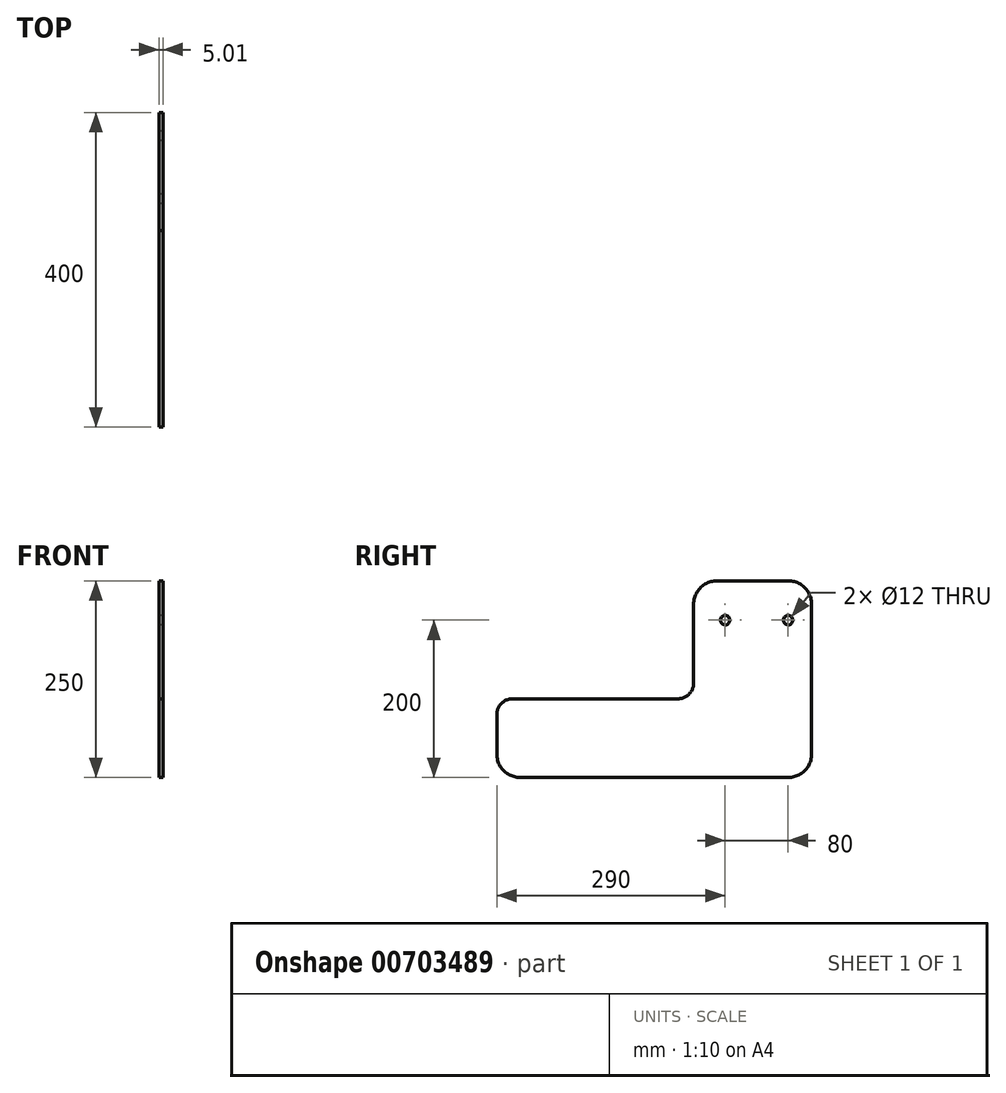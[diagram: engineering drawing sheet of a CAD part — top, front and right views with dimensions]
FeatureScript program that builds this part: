
annotation { "Feature Type Name" : "Feature", "Feature Type Description" : "" }
export const myFeature = defineFeature(function(context is Context, id is Id, definition is map)
    precondition{}
    {
        {
            var Q0;
            Q0=qCreatedBy(makeId("Top.planeOp"),FACE);
            var sketch = newSketch(context, id + "F0", { "sketchPlane" : qUnion([Q0])});
            skArc(sketch, "E0", {"start": v(-28.38, 31.77) * mm, "mid": v(-28.38, 31.77) * mm, "end": v(-28.38, 31.77) * mm});
            skLineSegment(sketch, "E1", {"start": v(-39.18, 36.77) * mm, "end": v(120.46, 36.77) * mm});
            skLineSegment(sketch, "E2", {"start": v(-54.54, 20.82) * mm, "end": v(-54.54, -83.23) * mm});
            skArc(sketch, "E3.0", {"start": v(-39.34, 31.77) * mm, "mid": v(-46.28, 29.18) * mm, "end": v(-49.54, 22.53) * mm});
            skLineSegment(sketch, "E4", {"start": v(-49.54, 22.53) * mm, "end": v(-49.54, -83.23) * mm});
            skLineSegment(sketch, "E5", {"start": v(-49.54, -83.23) * mm, "end": v(-54.54, -83.23) * mm});
            skLineSegment(sketch, "E6", {"start": v(-39.34, 31.77) * mm, "end": v(120.46, 31.77) * mm});
            skLineSegment(sketch, "E7", {"start": v(120.46, 31.77) * mm, "end": v(120.46, 36.77) * mm});
            skArc(sketch, "E8.trimOffspring", {"start": v(-49.54, 10.56) * mm, "mid": v(-49.54, 10.56) * mm, "end": v(-49.54, 10.56) * mm});
            skArc(sketch, "E9.trimOffspring", {"start": v(-39.18, 36.77) * mm, "mid": v(-50.37, 32.17) * mm, "end": v(-54.54, 20.82) * mm});
            skSolve(sketch);
        }
        {
            var Q0;
            Q0=qSketchRegion(id+"F0",true);
            extrude(context, id + "F1", {"entities" : qUnion([Q0]), "depth" : 120 * mm, "offsetDistance" : 25 * mm});
        }
        {
            var Q0;
            Q0=makeQuery(id+"F1.opExtrude","SWEPT_FACE",FACE,{"disambiguationData":[OSD([sQuery(id+"F0.wireOp",EDGE,"E1")])]});
            var sketch = newSketch(context, id + "F2", { "sketchPlane" : qUnion([Q0])});
            skCircle(sketch, "E10", {"center": v(-70.46, 60) * mm, "radius": 6 * mm});
            skCircle(sketch, "E11", {"center": v(-20.46, 60) * mm, "radius": 6 * mm});
            skSolve(sketch);
        }
        {
            var Q0;
            Q0=makeQuery(id+"F2.imprint","IMPRINT",FACE,{"disambiguationData":[TD([[makeQuery(id+"F2.imprint","IMPRINT",EDGE,{"derivedFrom":sQuery(id+"F2.wireOp",EDGE,"E10")}),1.0]])]});
            var Q1;
            Q1=makeQuery(id+"F2.imprint","IMPRINT",FACE,{"disambiguationData":[TD([[makeQuery(id+"F2.imprint","IMPRINT",EDGE,{"derivedFrom":sQuery(id+"F2.wireOp",EDGE,"E11")}),1.0]])]});
            var Q2;
            Q2=sQuery(id+"F2.wireOp",EDGE,"E11");
            var Q3;
            Q3=sQuery(id+"F2.wireOp",EDGE,"E10");
            extrude(context, id + "F3", {"entities" : qUnion([Q0, Q1]), "operationType" : NewBodyOperationType.REMOVE, "surfaceEntities" : qUnion([Q2, Q3]), "oppositeDirection" : true, "depth" : 5 * mm, "offsetDistance" : 25 * mm});
        }
        {
            var Q0;
            Q0=makeQuery(id+"F1.opExtrude","SWEPT_FACE",FACE,{"disambiguationData":[OSD([sQuery(id+"F0.wireOp",EDGE,"E4")])]});
            var sketch = newSketch(context, id + "F4", { "sketchPlane" : qUnion([Q0])});
            skLineSegment(sketch, "E12", {"start": v(-7.47, 160.68) * mm, "end": v(-347.47, 160.68) * mm});
            skLineSegment(sketch, "E13", {"start": v(-377.47, 190.68) * mm, "end": v(-377.47, 240.68) * mm});
            skLineSegment(sketch, "E14", {"start": v(-357.47, 260.68) * mm, "end": v(-147.47, 260.68) * mm});
            skLineSegment(sketch, "E15", {"start": v(-127.47, 280.68) * mm, "end": v(-127.47, 380.68) * mm});
            skLineSegment(sketch, "E16", {"start": v(-97.47, 410.68) * mm, "end": v(-7.47, 410.68) * mm});
            skLineSegment(sketch, "E17", {"start": v(22.53, 380.68) * mm, "end": v(22.53, 190.68) * mm});
            skPoint(sketch, "E18.visualSharp", {"position": v(-127.47, 410.68) * mm});
            skArc(sketch, "E18.filletArc", {"start": v(-97.47, 410.68) * mm, "mid": v(-118.68, 401.9) * mm, "end": v(-127.47, 380.68) * mm});
            skPoint(sketch, "E19.visualSharp", {"position": v(22.53, 410.68) * mm});
            skArc(sketch, "E19.filletArc", {"start": v(22.53, 380.68) * mm, "mid": v(13.74, 401.9) * mm, "end": v(-7.47, 410.68) * mm});
            skPoint(sketch, "E20.visualSharp", {"position": v(22.53, 160.68) * mm});
            skArc(sketch, "E20.filletArc", {"start": v(-7.47, 160.68) * mm, "mid": v(13.74, 169.47) * mm, "end": v(22.53, 190.68) * mm});
            skPoint(sketch, "E21.visualSharp", {"position": v(-377.47, 160.68) * mm});
            skArc(sketch, "E21.filletArc", {"start": v(-377.47, 190.68) * mm, "mid": v(-368.68, 169.47) * mm, "end": v(-347.47, 160.68) * mm});
            skPoint(sketch, "E22.visualSharp", {"position": v(-377.47, 260.68) * mm});
            skArc(sketch, "E22.filletArc", {"start": v(-357.47, 260.68) * mm, "mid": v(-371.61, 254.82) * mm, "end": v(-377.47, 240.68) * mm});
            skPoint(sketch, "E23.visualSharp", {"position": v(-127.47, 260.68) * mm});
            skArc(sketch, "E23.filletArc", {"start": v(-147.47, 260.68) * mm, "mid": v(-133.33, 266.54) * mm, "end": v(-127.47, 280.68) * mm});
            skCircle(sketch, "E24", {"center": v(-87.47, 360.68) * mm, "radius": 6 * mm});
            skCircle(sketch, "E25", {"center": v(-7.47, 360.68) * mm, "radius": 6 * mm});
            skSolve(sketch);
        }
        {
            var Q0;
            Q0=qSketchRegion(id+"F4",true);
            extrude(context, id + "F5", {"entities" : qUnion([Q0]), "depth" : 5 * mm, "offsetDistance" : 25 * mm});
        }
        {
            var Q0;
            Q0=makeQuery(id+"F1.opExtrude","SWEPT_BODY",BODY,{"disambiguationData":[OSD([sQuery(id+"F0.wireOp",EDGE,"E1"),sQuery(id+"F0.wireOp",EDGE,"E2"),sQuery(id+"F0.wireOp",EDGE,"E3.0"),sQuery(id+"F0.wireOp",EDGE,"E4"),sQuery(id+"F0.wireOp",EDGE,"E5"),sQuery(id+"F0.wireOp",EDGE,"E6"),sQuery(id+"F0.wireOp",EDGE,"E7"),sQuery(id+"F0.wireOp",EDGE,"E9.trimOffspring")])]});
            deleteBodies(context, id + "F6", {"entities" : qUnion([Q0])});
        }
    });
